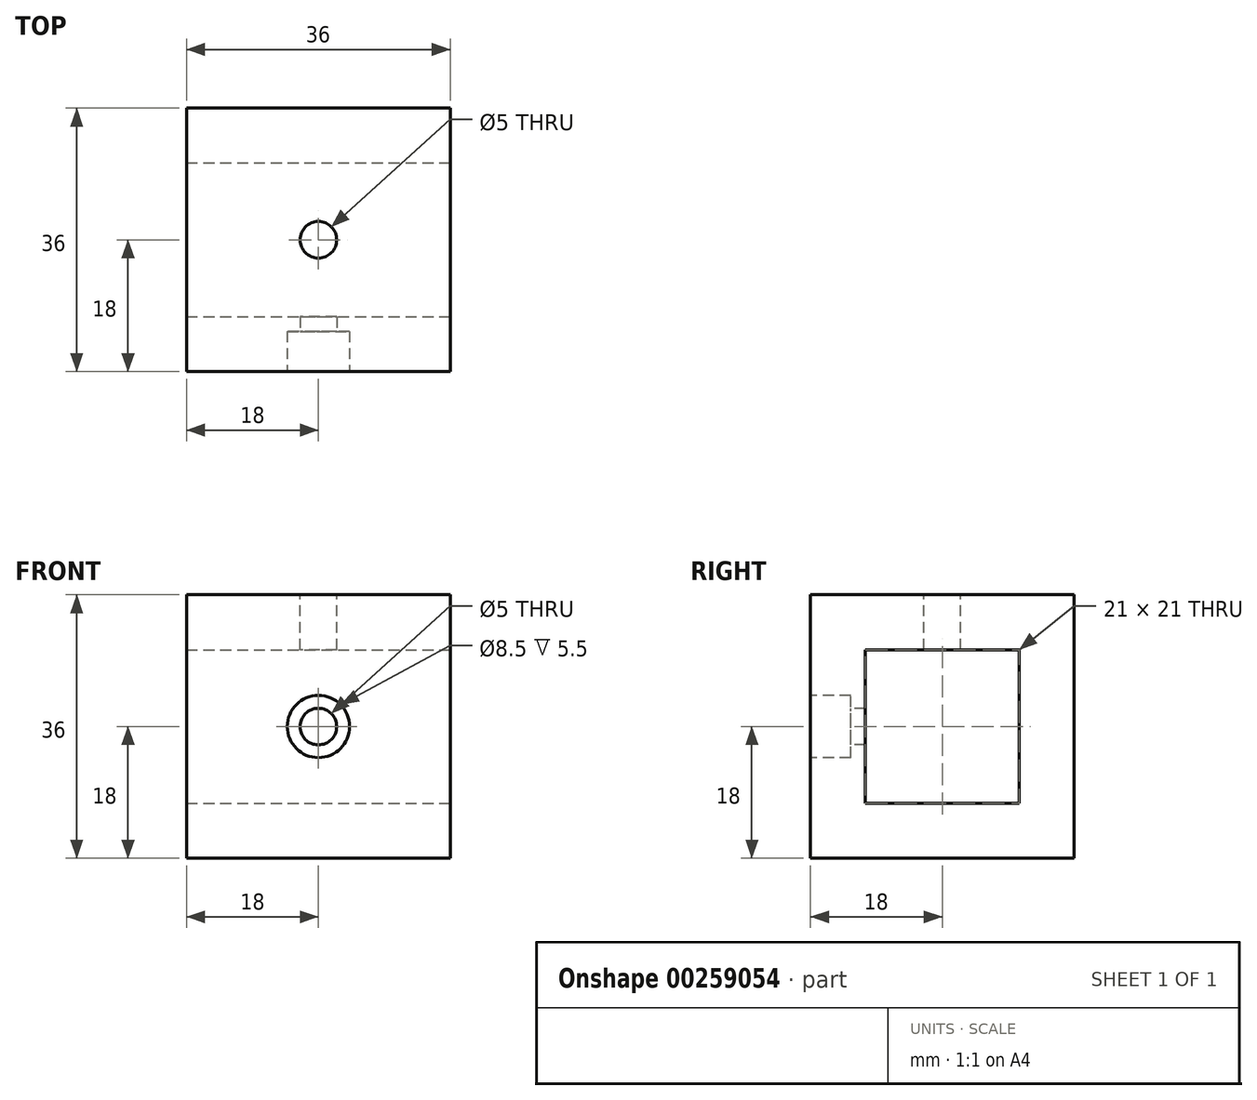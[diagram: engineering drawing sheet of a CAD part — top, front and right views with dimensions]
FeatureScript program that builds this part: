
annotation { "Feature Type Name" : "Feature", "Feature Type Description" : "" }
export const myFeature = defineFeature(function(context is Context, id is Id, definition is map)
    precondition{}
    {
        {
            var Q0;
            Q0=qCreatedBy(makeId("Front.planeOp"),FACE);
            var sketch = newSketch(context, id + "F0", { "sketchPlane" : qUnion([Q0])});
            skLineSegment(sketch, "E0.bottom", {"start": v(0, 0) * mm, "end": v(36, 0) * mm});
            skLineSegment(sketch, "E0.top", {"start": v(0, 36) * mm, "end": v(36, 36) * mm});
            skLineSegment(sketch, "E0.left", {"start": v(0, 0) * mm, "end": v(0, 36) * mm});
            skLineSegment(sketch, "E0.right", {"start": v(36, 0) * mm, "end": v(36, 36) * mm});
            skSolve(sketch);
        }
        {
            var Q0;
            Q0=makeQuery(id+"F0.imprint","IMPRINT",FACE,{"disambiguationData":[TD([[makeQuery(id+"F0.imprint","IMPRINT",EDGE,{"derivedFrom":sQuery(id+"F0.wireOp",EDGE,"E0.bottom")}),1.0]])]});
            extrude(context, id + "F1", {"entities" : qUnion([Q0]), "depth" : 36 * mm});
        }
        {
            var Q0;
            Q0=makeQuery(id+"F1.opExtrude","SWEPT_FACE",FACE,{"disambiguationData":[OSD([sQuery(id+"F0.wireOp",EDGE,"E0.right")])]});
            var sketch = newSketch(context, id + "F2", { "sketchPlane" : qUnion([Q0])});
            skLineSegment(sketch, "E1.bottom", {"start": v(-7.5, 28.5) * mm, "end": v(-28.5, 28.5) * mm});
            skLineSegment(sketch, "E1.top", {"start": v(-7.5, 7.5) * mm, "end": v(-28.5, 7.5) * mm});
            skLineSegment(sketch, "E1.left", {"start": v(-7.5, 28.5) * mm, "end": v(-7.5, 7.5) * mm});
            skLineSegment(sketch, "E1.right", {"start": v(-28.5, 28.5) * mm, "end": v(-28.5, 7.5) * mm});
            skSolve(sketch);
        }
        {
            var Q0;
            Q0 = qSketchRegion(id + "F2", true);
            extrude(context, id + "F3", {"entities" : qUnion([Q0]), "operationType" : NewBodyOperationType.REMOVE, "oppositeDirection" : true, "depth" : 60 * mm});
        }
        {
            var Q0;
            Q0=makeQuery(id+"F1.opExtrude","SWEPT_FACE",FACE,{"disambiguationData":[OSD([sQuery(id+"F0.wireOp",EDGE,"E0.top")])]});
            var sketch = newSketch(context, id + "F4", { "sketchPlane" : qUnion([Q0])});
            skCircle(sketch, "E2", {"center": v(18, -18) * mm, "radius": 2.5 * mm});
            skLineSegment(sketch, "E3", {"start": v(0, -18) * mm, "end": v(36, -18) * mm, "construction": true});
            skLineSegment(sketch, "E4", {"start": v(18, -36) * mm, "end": v(18, 0) * mm, "construction": true});
            skSolve(sketch);
        }
        {
            var Q0;
            Q0 = qSketchRegion(id + "F4", true);
            extrude(context, id + "F5", {"entities" : qUnion([Q0]), "operationType" : NewBodyOperationType.REMOVE, "oppositeDirection" : true, "depth" : 25 * mm});
        }
        {
            var Q0;
            Q0=makeQuery(id+"F1.opExtrude","CAP_FACE",FACE,{"disambiguationData":[OSD([sQuery(id+"F0.wireOp",EDGE,"E0.bottom"),sQuery(id+"F0.wireOp",EDGE,"E0.top"),sQuery(id+"F0.wireOp",EDGE,"E0.left"),sQuery(id+"F0.wireOp",EDGE,"E0.right")])],"isStart":false});
            var sketch = newSketch(context, id + "F6", { "sketchPlane" : qUnion([Q0])});
            skLineSegment(sketch, "E5", {"start": v(0, 18) * mm, "end": v(36, 18) * mm, "construction": true});
            skCircle(sketch, "E6", {"center": v(18, 18) * mm, "radius": 2.5 * mm});
            skSolve(sketch);
        }
        {
            var Q0;
            Q0 = qSketchRegion(id + "F6", true);
            extrude(context, id + "F7", {"entities" : qUnion([Q0]), "operationType" : NewBodyOperationType.REMOVE, "oppositeDirection" : true, "depth" : 20 * mm});
        }
        {
            var Q0;
            Q0=makeQuery(id+"F1.opExtrude","CAP_FACE",FACE,{"disambiguationData":[OSD([sQuery(id+"F0.wireOp",EDGE,"E0.bottom"),sQuery(id+"F0.wireOp",EDGE,"E0.top"),sQuery(id+"F0.wireOp",EDGE,"E0.left"),sQuery(id+"F0.wireOp",EDGE,"E0.right")])],"isStart":false});
            var sketch = newSketch(context, id + "F8", { "sketchPlane" : qUnion([Q0])});
            skCircle(sketch, "E7", {"center": v(18, 18) * mm, "radius": 4.25 * mm});
            skSolve(sketch);
        }
        {
            var Q0;
            Q0 = qSketchRegion(id + "F8", true);
            var Q1;
            Q1=sQuery(id+"F8.wireOp",EDGE,"E7");
            extrude(context, id + "F9", {"entities" : qUnion([Q0]), "operationType" : NewBodyOperationType.REMOVE, "surfaceEntities" : qUnion([Q1]), "oppositeDirection" : true, "depth" : 5.5 * mm});
        }
    });
